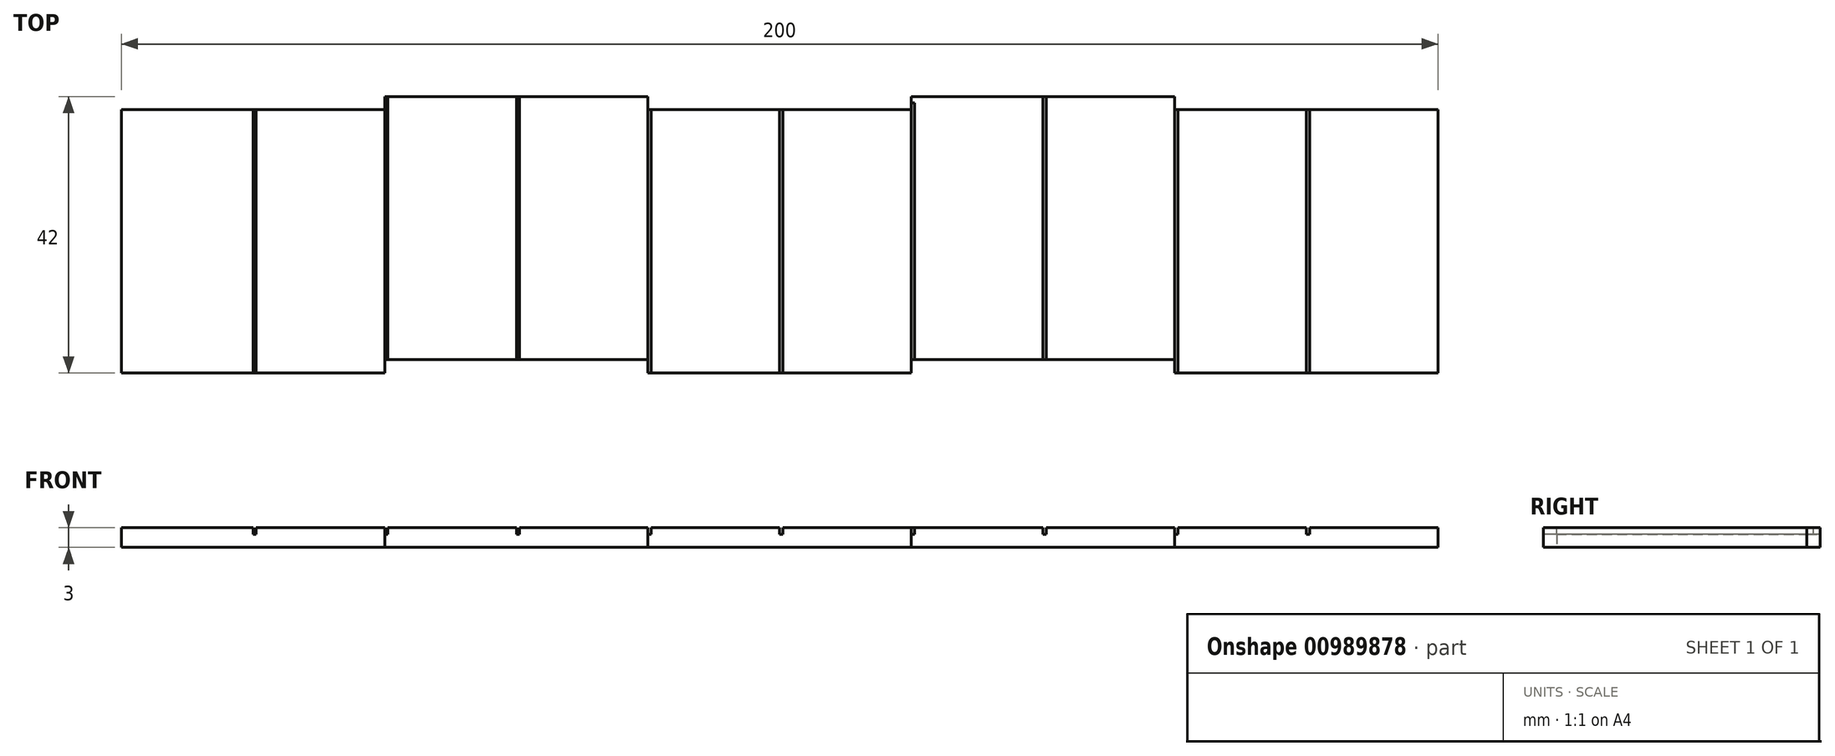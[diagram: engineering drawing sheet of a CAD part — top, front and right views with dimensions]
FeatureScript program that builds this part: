
annotation { "Feature Type Name" : "Feature", "Feature Type Description" : "" }
export const myFeature = defineFeature(function(context is Context, id is Id, definition is map)
    precondition{}
    {
        {
            var Q0;
            Q0=qCreatedBy(makeId("Top.planeOp"),FACE);
            var sketch = newSketch(context, id + "F0", { "sketchPlane" : qUnion([Q0])});
            skLineSegment(sketch, "E0.bottom", {"start": v(23.46, -20) * mm, "end": v(-16.54, -20) * mm});
            skLineSegment(sketch, "E0.top", {"start": v(23.46, 20) * mm, "end": v(-16.54, 20) * mm});
            skLineSegment(sketch, "E0.left", {"start": v(23.46, -20) * mm, "end": v(23.46, 20) * mm});
            skLineSegment(sketch, "E0.right", {"start": v(-16.54, -20) * mm, "end": v(-16.54, 20) * mm});
            skPoint(sketch, "E0.middle", {"position": v(3.46, 0) * mm});
            skLineSegment(sketch, "E1.bottom", {"start": v(63.46, -18) * mm, "end": v(23.46, -18) * mm});
            skLineSegment(sketch, "E1.top", {"start": v(63.46, 22) * mm, "end": v(23.46, 22) * mm});
            skLineSegment(sketch, "E1.left", {"start": v(63.46, -18) * mm, "end": v(63.46, 22) * mm});
            skLineSegment(sketch, "E1.right", {"start": v(23.46, -18) * mm, "end": v(23.46, 22) * mm});
            skLineSegment(sketch, "E2.bottom", {"start": v(103.46, -20) * mm, "end": v(63.46, -20) * mm});
            skLineSegment(sketch, "E2.top", {"start": v(103.46, 20) * mm, "end": v(63.46, 20) * mm});
            skLineSegment(sketch, "E2.left", {"start": v(103.46, -20) * mm, "end": v(103.46, 20) * mm});
            skLineSegment(sketch, "E2.right", {"start": v(63.46, -20) * mm, "end": v(63.46, 20) * mm});
            skLineSegment(sketch, "E3.bottom", {"start": v(143.46, -18) * mm, "end": v(103.46, -18) * mm});
            skLineSegment(sketch, "E3.top", {"start": v(143.46, 22) * mm, "end": v(103.46, 22) * mm});
            skLineSegment(sketch, "E3.left", {"start": v(143.46, -18) * mm, "end": v(143.46, 22) * mm});
            skLineSegment(sketch, "E3.right", {"start": v(103.46, -18) * mm, "end": v(103.46, 22) * mm});
            skLineSegment(sketch, "E4.bottom", {"start": v(183.46, -20) * mm, "end": v(143.46, -20) * mm});
            skLineSegment(sketch, "E4.top", {"start": v(183.46, 20) * mm, "end": v(143.46, 20) * mm});
            skLineSegment(sketch, "E4.left", {"start": v(183.46, -20) * mm, "end": v(183.46, 20) * mm});
            skLineSegment(sketch, "E4.right", {"start": v(143.46, -20) * mm, "end": v(143.46, 20) * mm});
            skSolve(sketch);
        }
        {
            var Q0;
            Q0=makeQuery(id+"F0.imprint","IMPRINT",FACE,{"disambiguationData":[TD([[makeQuery(id+"F0.imprint","IMPRINT",EDGE,{"derivedFrom":sQuery(id+"F0.wireOp",EDGE,"E0.bottom")}),-1.0]])]});
            var Q1;
            {var subQ2=sQuery(id+"F0.wireOp",EDGE,"E1.bottom");Q1=makeQuery(id+"F0.imprint","IMPRINT",FACE,{"disambiguationData":[TD([[makeQuery(id+"F0.imprint","IMPRINT",EDGE,{"derivedFrom":subQ2}),-1.0]])]});}
            var Q2;
            {var subQ2=sQuery(id+"F0.wireOp",EDGE,"E2.bottom");Q2=makeQuery(id+"F0.imprint","IMPRINT",FACE,{"disambiguationData":[TD([[makeQuery(id+"F0.imprint","IMPRINT",EDGE,{"derivedFrom":subQ2}),-1.0]])]});}
            var Q3;
            {var subQ2=sQuery(id+"F0.wireOp",EDGE,"E3.bottom");Q3=makeQuery(id+"F0.imprint","IMPRINT",FACE,{"disambiguationData":[TD([[makeQuery(id+"F0.imprint","IMPRINT",EDGE,{"derivedFrom":subQ2}),-1.0]])]});}
            var Q4;
            {var subQ2=sQuery(id+"F0.wireOp",EDGE,"E4.bottom");Q4=makeQuery(id+"F0.imprint","IMPRINT",FACE,{"disambiguationData":[TD([[makeQuery(id+"F0.imprint","IMPRINT",EDGE,{"derivedFrom":subQ2}),-1.0]])]});}
            extrude(context, id + "F1", {"entities" : qUnion([Q0, Q1, Q2, Q3, Q4]), "depth" : 3 * mm, "offsetDistance" : 25 * mm});
        }
        {
            var Q0;
            Q0=makeQuery(id+"F1.opExtrude","CAP_FACE",FACE,{"disambiguationData":[OSD([sQuery(id+"F0.wireOp",EDGE,"E0.bottom"),sQuery(id+"F0.wireOp",EDGE,"E0.top"),sQuery(id+"F0.wireOp",EDGE,"E0.left"),sQuery(id+"F0.wireOp",EDGE,"E0.right"),sQuery(id+"F0.wireOp",EDGE,"E1.bottom"),sQuery(id+"F0.wireOp",EDGE,"E1.top"),sQuery(id+"F0.wireOp",EDGE,"E1.left"),sQuery(id+"F0.wireOp",EDGE,"E1.right"),sQuery(id+"F0.wireOp",EDGE,"E2.bottom"),sQuery(id+"F0.wireOp",EDGE,"E2.top"),sQuery(id+"F0.wireOp",EDGE,"E2.left"),sQuery(id+"F0.wireOp",EDGE,"E2.right"),sQuery(id+"F0.wireOp",EDGE,"E3.bottom"),sQuery(id+"F0.wireOp",EDGE,"E3.top"),sQuery(id+"F0.wireOp",EDGE,"E3.left"),sQuery(id+"F0.wireOp",EDGE,"E3.right"),sQuery(id+"F0.wireOp",EDGE,"E4.bottom"),sQuery(id+"F0.wireOp",EDGE,"E4.top"),sQuery(id+"F0.wireOp",EDGE,"E4.left"),sQuery(id+"F0.wireOp",EDGE,"E4.right")])],"isStart":false});
            var sketch = newSketch(context, id + "F2", { "sketchPlane" : qUnion([Q0])});
            skLineSegment(sketch, "E5.bottom", {"start": v(3.46, 21) * mm, "end": v(3.96, 21) * mm});
            skLineSegment(sketch, "E5.top", {"start": v(3.46, -20) * mm, "end": v(3.96, -20) * mm});
            skLineSegment(sketch, "E5.left", {"start": v(3.46, 21) * mm, "end": v(3.46, -20) * mm});
            skLineSegment(sketch, "E5.right", {"start": v(3.96, 21) * mm, "end": v(3.96, -20) * mm});
            skLineSegment(sketch, "E6.bottom", {"start": v(43.46, 23) * mm, "end": v(43.96, 23) * mm});
            skLineSegment(sketch, "E6.top", {"start": v(43.46, -18) * mm, "end": v(43.96, -18) * mm});
            skLineSegment(sketch, "E6.left", {"start": v(43.46, 23) * mm, "end": v(43.46, -18) * mm});
            skLineSegment(sketch, "E6.right", {"start": v(43.96, 23) * mm, "end": v(43.96, -18) * mm});
            skLineSegment(sketch, "E7.bottom", {"start": v(23.46, 23) * mm, "end": v(23.96, 23) * mm});
            skLineSegment(sketch, "E7.top", {"start": v(23.46, -18) * mm, "end": v(23.96, -18) * mm});
            skLineSegment(sketch, "E7.left", {"start": v(23.46, 23) * mm, "end": v(23.46, -18) * mm});
            skLineSegment(sketch, "E7.right", {"start": v(23.96, 23) * mm, "end": v(23.96, -18) * mm});
            skLineSegment(sketch, "E8.bottom", {"start": v(63.46, 21) * mm, "end": v(63.96, 21) * mm});
            skLineSegment(sketch, "E8.top", {"start": v(63.46, -20) * mm, "end": v(63.96, -20) * mm});
            skLineSegment(sketch, "E8.left", {"start": v(63.46, 21) * mm, "end": v(63.46, -20) * mm});
            skLineSegment(sketch, "E8.right", {"start": v(63.96, 21) * mm, "end": v(63.96, -20) * mm});
            skLineSegment(sketch, "E9.bottom", {"start": v(83.46, 21) * mm, "end": v(83.96, 21) * mm});
            skLineSegment(sketch, "E9.top", {"start": v(83.46, -20) * mm, "end": v(83.96, -20) * mm});
            skLineSegment(sketch, "E9.left", {"start": v(83.46, 21) * mm, "end": v(83.46, -20) * mm});
            skLineSegment(sketch, "E9.right", {"start": v(83.96, 21) * mm, "end": v(83.96, -20) * mm});
            skLineSegment(sketch, "E10.bottom", {"start": v(103.46, 21) * mm, "end": v(103.96, 21) * mm});
            skLineSegment(sketch, "E10.top", {"start": v(103.46, -20) * mm, "end": v(103.96, -20) * mm});
            skLineSegment(sketch, "E10.left", {"start": v(103.46, 21) * mm, "end": v(103.46, -20) * mm});
            skLineSegment(sketch, "E10.right", {"start": v(103.96, 21) * mm, "end": v(103.96, -20) * mm});
            skLineSegment(sketch, "E11.bottom", {"start": v(123.46, 22.88) * mm, "end": v(123.96, 22.88) * mm});
            skLineSegment(sketch, "E11.top", {"start": v(123.46, -18.1) * mm, "end": v(123.96, -18.1) * mm});
            skLineSegment(sketch, "E11.left", {"start": v(123.46, 22.88) * mm, "end": v(123.46, -18.1) * mm});
            skLineSegment(sketch, "E11.right", {"start": v(123.96, 22.88) * mm, "end": v(123.96, -18.1) * mm});
            skLineSegment(sketch, "E12.bottom", {"start": v(143.46, 21) * mm, "end": v(143.96, 21) * mm});
            skLineSegment(sketch, "E12.top", {"start": v(143.46, -20) * mm, "end": v(143.96, -20) * mm});
            skLineSegment(sketch, "E12.left", {"start": v(143.46, 21) * mm, "end": v(143.46, -20) * mm});
            skLineSegment(sketch, "E12.right", {"start": v(143.96, 21) * mm, "end": v(143.96, -20) * mm});
            skLineSegment(sketch, "E13.bottom", {"start": v(163.46, 21) * mm, "end": v(163.96, 21) * mm});
            skLineSegment(sketch, "E13.top", {"start": v(163.46, -20) * mm, "end": v(163.96, -20) * mm});
            skLineSegment(sketch, "E13.left", {"start": v(163.46, 21) * mm, "end": v(163.46, -20) * mm});
            skLineSegment(sketch, "E13.right", {"start": v(163.96, 21) * mm, "end": v(163.96, -20) * mm});
            skSolve(sketch);
        }
        {
            var Q0;
            {var subQ0=sQuery(id+"F2.wireOp",EDGE,"E5.top");Q0=makeQuery(id+"F2.imprint","IMPRINT",FACE,{"disambiguationData":[TD([[makeQuery(id+"F2.imprint","IMPRINT",EDGE,{"derivedFrom":subQ0}),-1.0]])]});}
            var Q1;
            {var subQ2=sQuery(id+"F2.wireOp",EDGE,"E7.top");Q1=makeQuery(id+"F2.imprint","IMPRINT",FACE,{"disambiguationData":[TD([[makeQuery(id+"F2.imprint","IMPRINT",EDGE,{"derivedFrom":subQ2}),-1.0]])]});}
            var Q2;
            {var subQ0=sQuery(id+"F2.wireOp",EDGE,"E6.top");Q2=makeQuery(id+"F2.imprint","IMPRINT",FACE,{"disambiguationData":[TD([[makeQuery(id+"F2.imprint","IMPRINT",EDGE,{"derivedFrom":subQ0}),-1.0]])]});}
            var Q3;
            {var subQ4=sQuery(id+"F2.wireOp",EDGE,"E8.top");Q3=makeQuery(id+"F2.imprint","IMPRINT",FACE,{"disambiguationData":[TD([[makeQuery(id+"F2.imprint","IMPRINT",EDGE,{"derivedFrom":subQ4}),-1.0]])]});}
            var Q4;
            {var subQ0=sQuery(id+"F2.wireOp",EDGE,"E9.top");Q4=makeQuery(id+"F2.imprint","IMPRINT",FACE,{"disambiguationData":[TD([[makeQuery(id+"F2.imprint","IMPRINT",EDGE,{"derivedFrom":subQ0}),-1.0]])]});}
            var Q5;
            {var subQ4=sQuery(id+"F2.wireOp",EDGE,"E10.bottom");Q5=makeQuery(id+"F2.imprint","IMPRINT",FACE,{"disambiguationData":[TD([[makeQuery(id+"F2.imprint","IMPRINT",EDGE,{"derivedFrom":subQ4}),-1.0]])]});}
            var Q6;
            {var subQ0=sQuery(id+"F2.wireOp",EDGE,"E11.left");var subQ1=makeQuery(id+"F1.opExtrude","CAP_EDGE",EDGE,{"disambiguationData":[OSD([sQuery(id+"F0.wireOp",EDGE,"E3.top")])],"isStart":false});var subQ2=makeQuery(id+"F2.imprint","INTERSECT",VERTEX,{"derivedFrom":[subQ1,subQ0]});Q6=makeQuery(id+"F2.imprint","IMPRINT",FACE,{"disambiguationData":[TD([[makeQuery(id+"F2.imprint","IMPRINT",EDGE,{"disambiguationData":[TD([[subQ2,-1.0]])],"derivedFrom":subQ0}),1.0]])]});}
            var Q7;
            {var subQ4=sQuery(id+"F2.wireOp",EDGE,"E12.top");Q7=makeQuery(id+"F2.imprint","IMPRINT",FACE,{"disambiguationData":[TD([[makeQuery(id+"F2.imprint","IMPRINT",EDGE,{"derivedFrom":subQ4}),-1.0]])]});}
            var Q8;
            {var subQ0=sQuery(id+"F2.wireOp",EDGE,"E13.top");Q8=makeQuery(id+"F2.imprint","IMPRINT",FACE,{"disambiguationData":[TD([[makeQuery(id+"F2.imprint","IMPRINT",EDGE,{"derivedFrom":subQ0}),-1.0]])]});}
            var Q9;
            Q9=sQuery(id+"F2.wireOp",EDGE,"E5.left");
            var Q10;
            Q10=sQuery(id+"F2.wireOp",EDGE,"E5.right");
            var Q11;
            Q11=sQuery(id+"F2.wireOp",EDGE,"E5.top");
            var Q12;
            Q12=sQuery(id+"F2.wireOp",EDGE,"E5.bottom");
            extrude(context, id + "F3", {"entities" : qUnion([Q0, Q1, Q2, Q3, Q4, Q5, Q6, Q7, Q8]), "operationType" : NewBodyOperationType.REMOVE, "surfaceEntities" : qUnion([Q9, Q10, Q11, Q12]), "oppositeDirection" : true, "depth" : 1 * mm, "offsetDistance" : 25 * mm});
        }
    });
